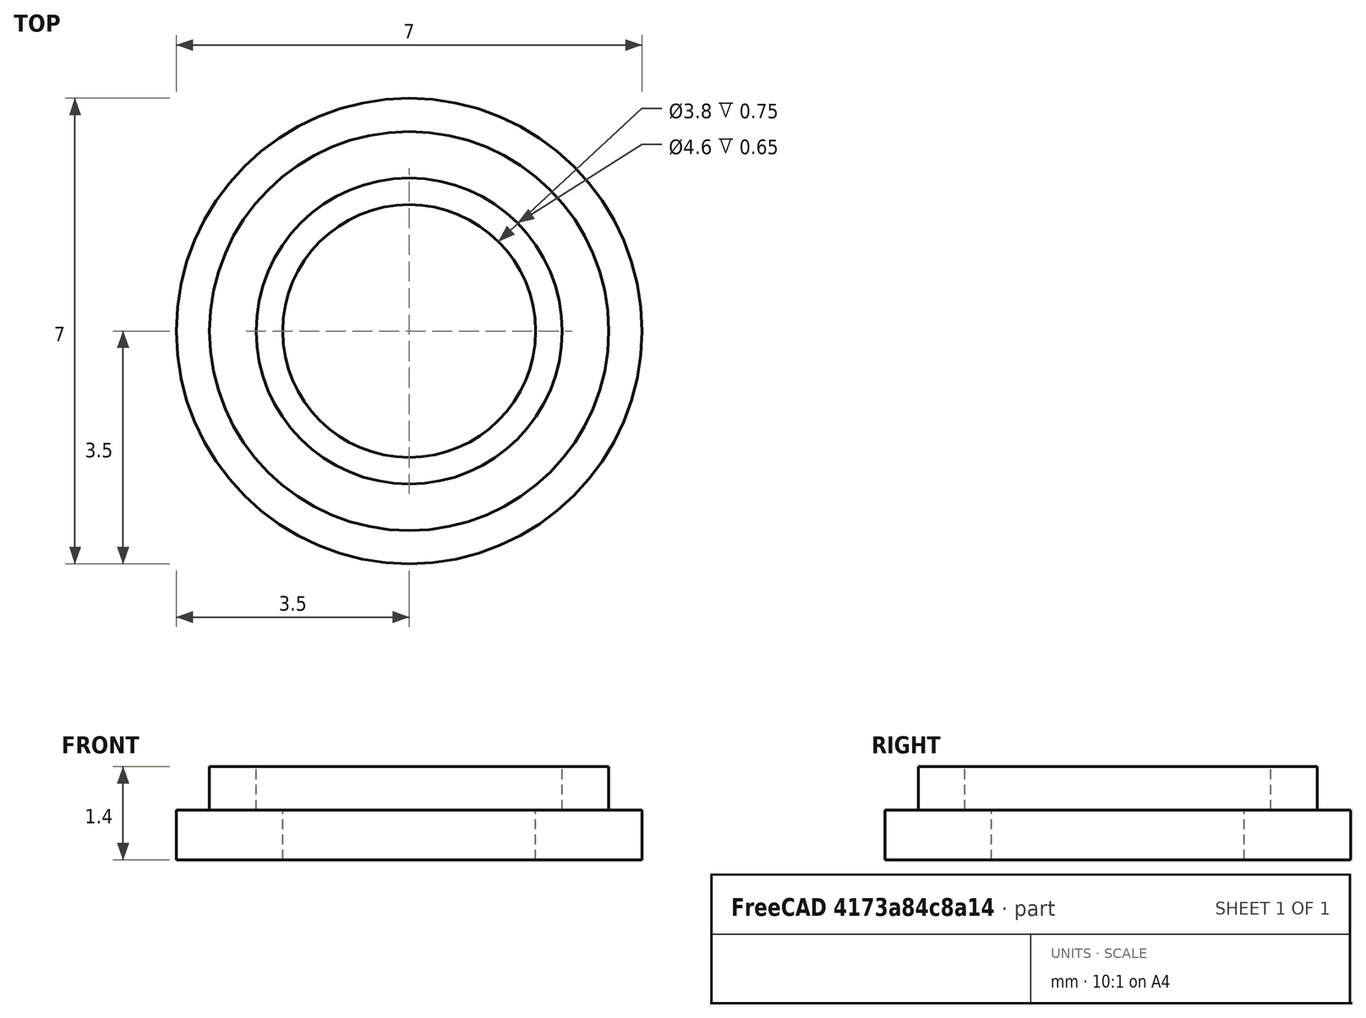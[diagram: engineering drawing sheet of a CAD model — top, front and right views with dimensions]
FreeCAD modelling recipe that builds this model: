
FCSTD DOCUMENT  (FreeCAD 0.18.4R)
Label: ScrewGasket3
License: All rights reserved
LicenseURL: http://en.wikipedia.org/wiki/All_rights_reserved
objects: Part::Cylinder×4, Part::Cut×2, Part::MultiFuse×1, Mesh::Feature×1
note: 7 computed .brp shape members not serialized (recipe doc carries the construction recipe); baked Part::Feature solids carry a one-line shape summary decoded from their .brp

FEATURE [Part::Cylinder] Cylinder  label="Zylinder"
  Angle = 360
  AttacherType = Attacher::AttachEngine3D
  Height = 0.75
  Radius = 3.5
FEATURE [Part::Cylinder] Cylinder001  label="Zylinder001"
  Angle = 360
  AttacherType = Attacher::AttachEngine3D
  Height = 1
  Placement = pos=(0,0,-0.2) rot=(0,0,1;0rad)
  Radius = 1.9
FEATURE [Part::Cut] Cut
  Base = -> Cylinder
  Tool = -> Cylinder001
FEATURE [Part::Cylinder] Cylinder002  label="Zylinder002"
  Angle = 360
  AttacherType = Attacher::AttachEngine3D
  Height = 1
  Placement = pos=(0,0,0.4) rot=(0,0,1;0rad)
  Radius = 3
FEATURE [Part::Cylinder] Cylinder003  label="Zylinder003"
  Angle = 360
  AttacherType = Attacher::AttachEngine3D
  Height = 10
  Radius = 2.3
FEATURE [Part::Cut] Cut001
  Base = -> Cylinder002
  Tool = -> Cylinder003
FEATURE [Part::MultiFuse] Fusion
  Shapes = -> [Cut,Cut001]
FEATURE [Mesh::Feature] Mesh  label="Fusion (Meshed)"
